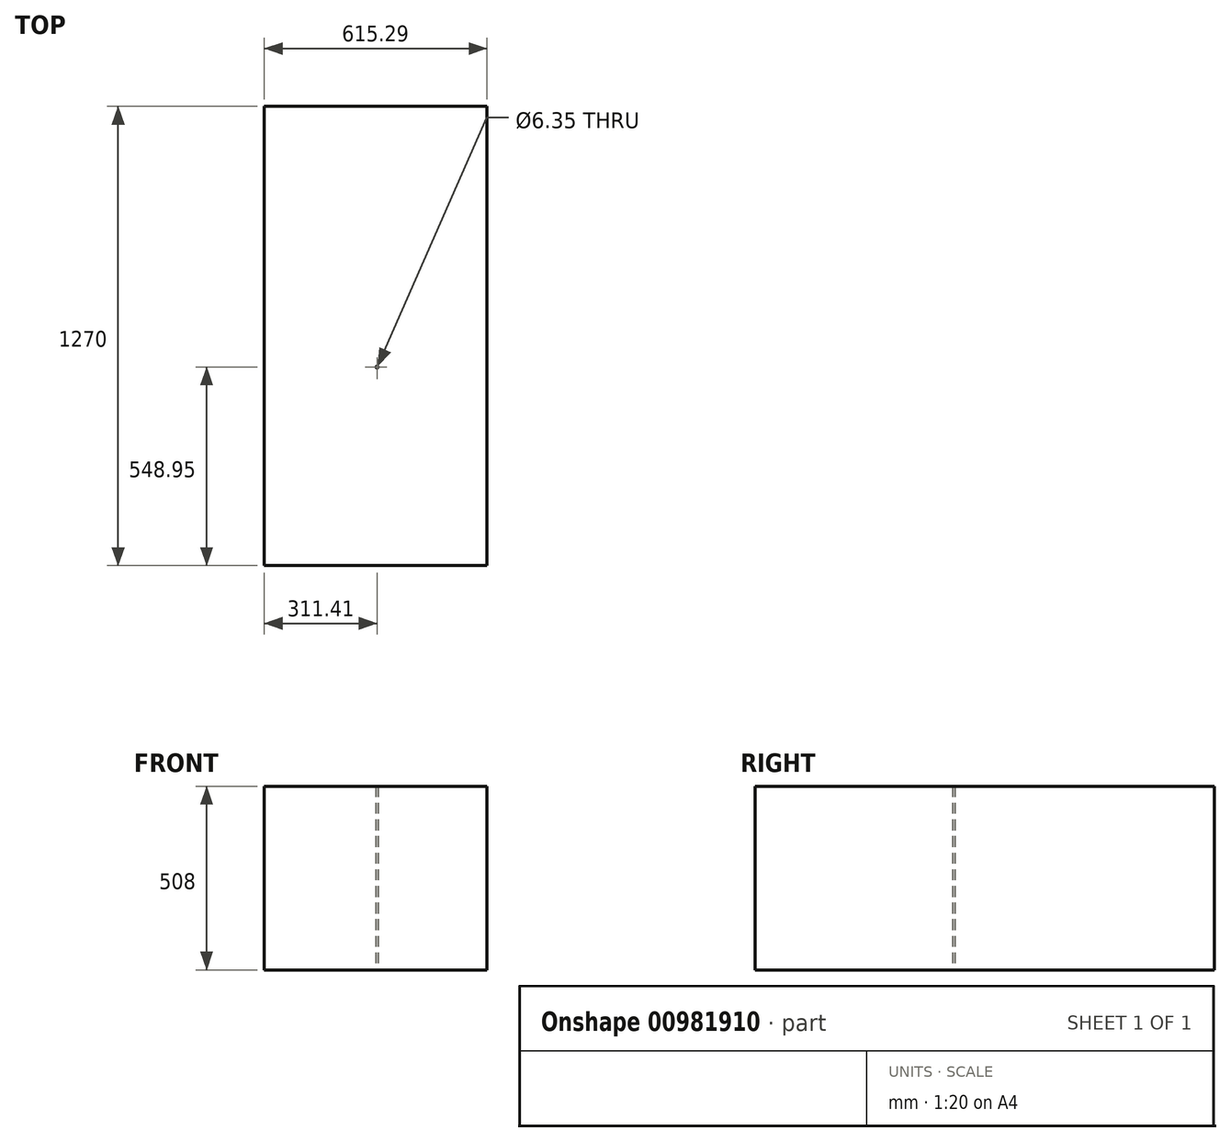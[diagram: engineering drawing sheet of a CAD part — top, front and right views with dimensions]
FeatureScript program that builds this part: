
annotation { "Feature Type Name" : "Feature", "Feature Type Description" : "" }
export const myFeature = defineFeature(function(context is Context, id is Id, definition is map)
    precondition{}
    {
        {
            var Q0;
            Q0=qCreatedBy(makeId("Top.planeOp"),FACE);
            var sketch = newSketch(context, id + "F0", { "sketchPlane" : qUnion([Q0])});
            skLineSegment(sketch, "E0.bottom", {"start": v(303.88, -548.95) * mm, "end": v(-311.4, -548.95) * mm});
            skLineSegment(sketch, "E0.top", {"start": v(303.88, 721.05) * mm, "end": v(-311.4, 721.05) * mm});
            skLineSegment(sketch, "E0.left", {"start": v(303.88, -548.95) * mm, "end": v(303.88, 721.05) * mm});
            skLineSegment(sketch, "E0.right", {"start": v(-311.4, -548.95) * mm, "end": v(-311.4, 721.05) * mm});
            skPoint(sketch, "E0.middle", {"position": v(-3.77, 86.05) * mm});
            skSolve(sketch);
        }
        {
            var Q0;
            Q0=makeQuery(id+"F0.imprint","IMPRINT",FACE,{"disambiguationData":[TD([[makeQuery(id+"F0.imprint","IMPRINT",EDGE,{"derivedFrom":sQuery(id+"F0.wireOp",EDGE,"E0.bottom")}),-1.0]])]});
            extrude(context, id + "F1", {"entities" : qUnion([Q0]), "depth" : 508 * mm, "offsetDistance" : 25.4 * mm});
        }
        {
            var Q0;
            Q0=makeQuery(id+"F1.opExtrude","CAP_FACE",FACE,{"disambiguationData":[OSD([sQuery(id+"F0.wireOp",EDGE,"E0.bottom"),sQuery(id+"F0.wireOp",EDGE,"E0.top"),sQuery(id+"F0.wireOp",EDGE,"E0.left"),sQuery(id+"F0.wireOp",EDGE,"E0.right")])],"isStart":true});
            var sketch = newSketch(context, id + "F2", { "sketchPlane" : qUnion([Q0])});
            skCircle(sketch, "E1", {"center": v(0, 0) * mm, "radius": 273.66 * mm});
            skSolve(sketch);
        }
        {
            var Q0;
            Q0=sQuery(id+"F2.wireOp",VERTEX,"E1.center");
            var Q1;
            Q1=makeQuery(id+"F1.opExtrude","SWEPT_BODY",BODY,{"disambiguationData":[OSD([sQuery(id+"F0.wireOp",EDGE,"E0.bottom"),sQuery(id+"F0.wireOp",EDGE,"E0.top"),sQuery(id+"F0.wireOp",EDGE,"E0.left"),sQuery(id+"F0.wireOp",EDGE,"E0.right")])]});
            hole(context, id + "F3", {"style" : HoleStyle.SIMPLE, "endStyle" : HoleEndStyle.THROUGH, "holeDiameter" : 6.35 * mm, "majorDiameter" : 6.35 * mm, "isTappedThrough" : true, "tappedDepth" : 12.7 * mm, "tapClearance" : 3, "locations" : qUnion([Q0]), "scope" : qUnion([Q1])});
        }
    });
